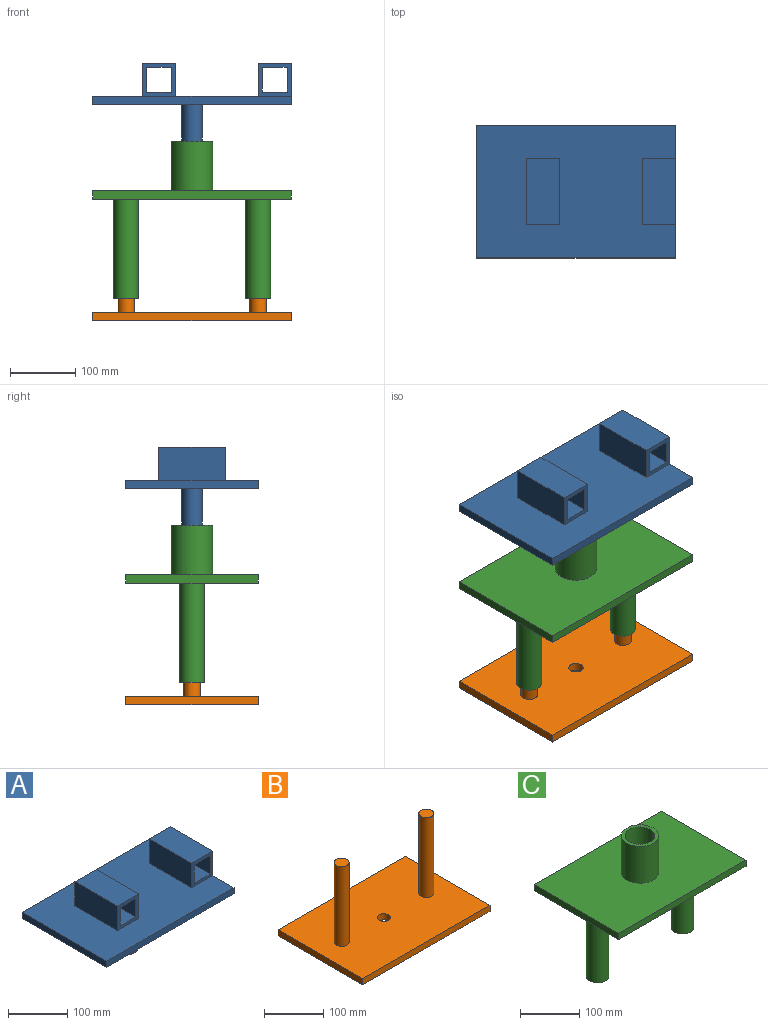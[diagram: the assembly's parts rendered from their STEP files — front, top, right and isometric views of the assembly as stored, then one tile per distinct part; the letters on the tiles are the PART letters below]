
ASSEMBLY  parts=3 mates=2
PART A: 25 faces, bbox 304.8x203.2x152.4 mm
  f0: plane 50.8x50.8mm, normal (0,-1,0), area 1129mm2, adj f4,f8,f15,f16,f21,f22,f23,f24
  f1: plane 50.8x50.8mm, normal (0,1,0), area 1129mm2, adj f4,f8,f15,f16,f21,f22,f23,f24
  f2: plane 50.8x50.8mm, normal (0,-1,0), area 1129mm2, adj f4,f12,f13,f14,f17,f18,f19,f20
  f3: plane 50.8x50.8mm, normal (0,1,0), area 1129mm2, adj f4,f12,f13,f14,f17,f18,f19,f20
  f4: plane 304.8x203.2mm, normal (0,0,1), area 51612.8mm2, adj f0,f1,f2,f3,f7,f8,f9,f10
  f5: cylinder r=15.88mm len=88.9mm, axis (0,0,-1), area 8867.4mm2, adj f6,f11
  f6: plane 31.75x31.75mm, normal (0,0,-1), area 791.7mm2, adj f5
  f7: plane 304.8x12.7mm, normal (0,-1,0), area 3871mm2, adj f4,f8,f10,f11
  f8: plane 203.2x63.5mm, normal (1,0,0), area 7741.9mm2, adj f0,f1,f4,f7,f9,f11,f16
  f9: plane 304.8x12.7mm, normal (0,1,0), area 3871mm2, adj f4,f8,f10,f11
  f10: plane 203.2x12.7mm, normal (-1,0,0), area 2580.6mm2, adj f4,f7,f9,f11
  f11: plane 304.8x203.2mm, normal (0,0,-1), area 61143.6mm2, adj f5,f7,f8,f9,f10
  f12: plane 101.6x50.8mm, normal (1,0,0), area 5161.3mm2, adj f2,f3,f4,f14
  f13: plane 101.6x50.8mm, normal (-1,0,0), area 5161.3mm2, adj f2,f3,f4,f14
  f14: plane 101.6x50.8mm, normal (0,0,1), area 5161.3mm2, adj f2,f3,f12,f13
  f15: plane 101.6x50.8mm, normal (-1,0,0), area 5161.3mm2, adj f0,f1,f4,f16
  f16: plane 101.6x50.8mm, normal (0,0,1), area 5161.3mm2, adj f0,f1,f8,f15
  f17: plane 101.6x38.1mm, normal (1,0,0), area 3871mm2, adj f2,f3,f18,f20
  f18: plane 101.6x38.1mm, normal (0,0,1), area 3871mm2, adj f2,f3,f17,f19
  f19: plane 101.6x38.1mm, normal (-1,0,0), area 3871mm2, adj f2,f3,f18,f20
  f20: plane 101.6x38.1mm, normal (0,0,-1), area 3871mm2, adj f2,f3,f17,f19
  f21: plane 101.6x38.1mm, normal (0,0,1), area 3871mm2, adj f0,f1,f22,f24
  f22: plane 101.6x38.1mm, normal (-1,0,0), area 3871mm2, adj f0,f1,f21,f23
  f23: plane 101.6x38.1mm, normal (0,0,-1), area 3871mm2, adj f0,f1,f22,f24
  f24: plane 101.6x38.1mm, normal (1,0,0), area 3871mm2, adj f0,f1,f21,f23
PART B: 11 faces, bbox 304.8x203.2x177.8 mm
  f0: plane 304.8x203.2mm, normal (0,0,-1), area 61547.4mm2, adj f1,f3,f4,f5,f10
  f1: plane 203.2x12.7mm, normal (1,0,0), area 2580.6mm2, adj f0,f2,f4,f5
  f2: plane 304.8x203.2mm, normal (0,0,1), area 60534mm2, adj f1,f3,f4,f5,f6,f8,f10
  f3: plane 203.2x12.7mm, normal (-1,0,0), area 2580.6mm2, adj f0,f2,f4,f5
  f4: plane 304.8x12.7mm, normal (0,-1,0), area 3871mm2, adj f0,f1,f2,f3
  f5: plane 304.8x12.7mm, normal (0,1,0), area 3871mm2, adj f0,f1,f2,f3
  f6: cylinder r=12.7mm len=165.1mm, axis (0,0,-1), area 13174.4mm2, adj f2,f7
  f7: plane 25.4x25.4mm, normal (0,0,1), area 506.7mm2, adj f6
  f8: cylinder r=12.7mm len=165.1mm, axis (0,0,-1), area 13174.4mm2, adj f2,f9
  f9: plane 25.4x25.4mm, normal (0,0,1), area 506.7mm2, adj f8
  f10: cylinder r=11.11mm len=22.23mm, axis (0,0,1), area 886.7mm2, adj f0,f2
PART C: 19 faces, bbox 304.8x203.2x241.3 mm
  f0: plane 50.8x50.8mm, normal (0,0,1), area 1929.8mm2, adj f15,f16
  f1: plane 304.8x203.2mm, normal (0,0,-1), area 59558.2mm2, adj f2,f4,f5,f6,f8,f11,f15
  f2: plane 203.2x12.7mm, normal (1,0,0), area 2580.6mm2, adj f1,f3,f5,f6
  f3: plane 304.8x203.2mm, normal (0,0,1), area 58768.4mm2, adj f2,f4,f5,f6,f17
  f4: plane 203.2x12.7mm, normal (-1,0,0), area 2580.6mm2, adj f1,f3,f5,f6
  f5: plane 304.8x12.7mm, normal (0,-1,0), area 3871mm2, adj f1,f2,f3,f4
  f6: plane 304.8x12.7mm, normal (0,1,0), area 3871mm2, adj f1,f2,f3,f4
  f7: cylinder r=13.33mm len=152.4mm, axis (0,0,1), area 12769mm2, adj f9,f10
  f8: cylinder r=19.05mm len=152.4mm, axis (0,0,1), area 18241.5mm2, adj f1,f9
  f9: plane 38.1x38.1mm, normal (0,0,-1), area 581.4mm2, adj f7,f8
  f10: plane 26.67x26.67mm, normal (0,0,-1), area 558.6mm2, adj f7
  f11: cylinder r=19.05mm len=152.4mm, axis (0,0,1), area 18241.5mm2, adj f1,f13
  f12: cylinder r=13.33mm len=152.4mm, axis (0,0,1), area 12769mm2, adj f13,f14
  f13: plane 38.1x38.1mm, normal (0,0,-1), area 581.4mm2, adj f11,f12
  f14: plane 26.67x26.67mm, normal (0,0,-1), area 558.6mm2, adj f12
  f15: cylinder r=5.56mm len=12.7mm, axis (0,0,1), area 443.4mm2, adj f0,f1
  f16: cylinder r=25.4mm len=76.2mm, axis (0,0,-1), area 12161mm2, adj f0,f18
  f17: cylinder r=31.75mm len=76.2mm, axis (0,0,-1), area 15201.2mm2, adj f3,f18
  f18: plane 63.5x63.5mm, normal (0,0,1), area 1140.1mm2, adj f16,f17
PLACE A t=(-101.78,433.59,267.99)mm
PLACE B t=(-101.78,433.59,30.95)mm
PLACE C t=(-101.78,433.59,217.97)mm
MATE cylindrical A.f5 <-> C.f15  axis (0,0,-1) through (-101.78,433.59,267.99)mm
MATE cylindrical B.f6 <-> C.f11  axis (0,0,-1) through (-203.38,433.59,202.4)mm
